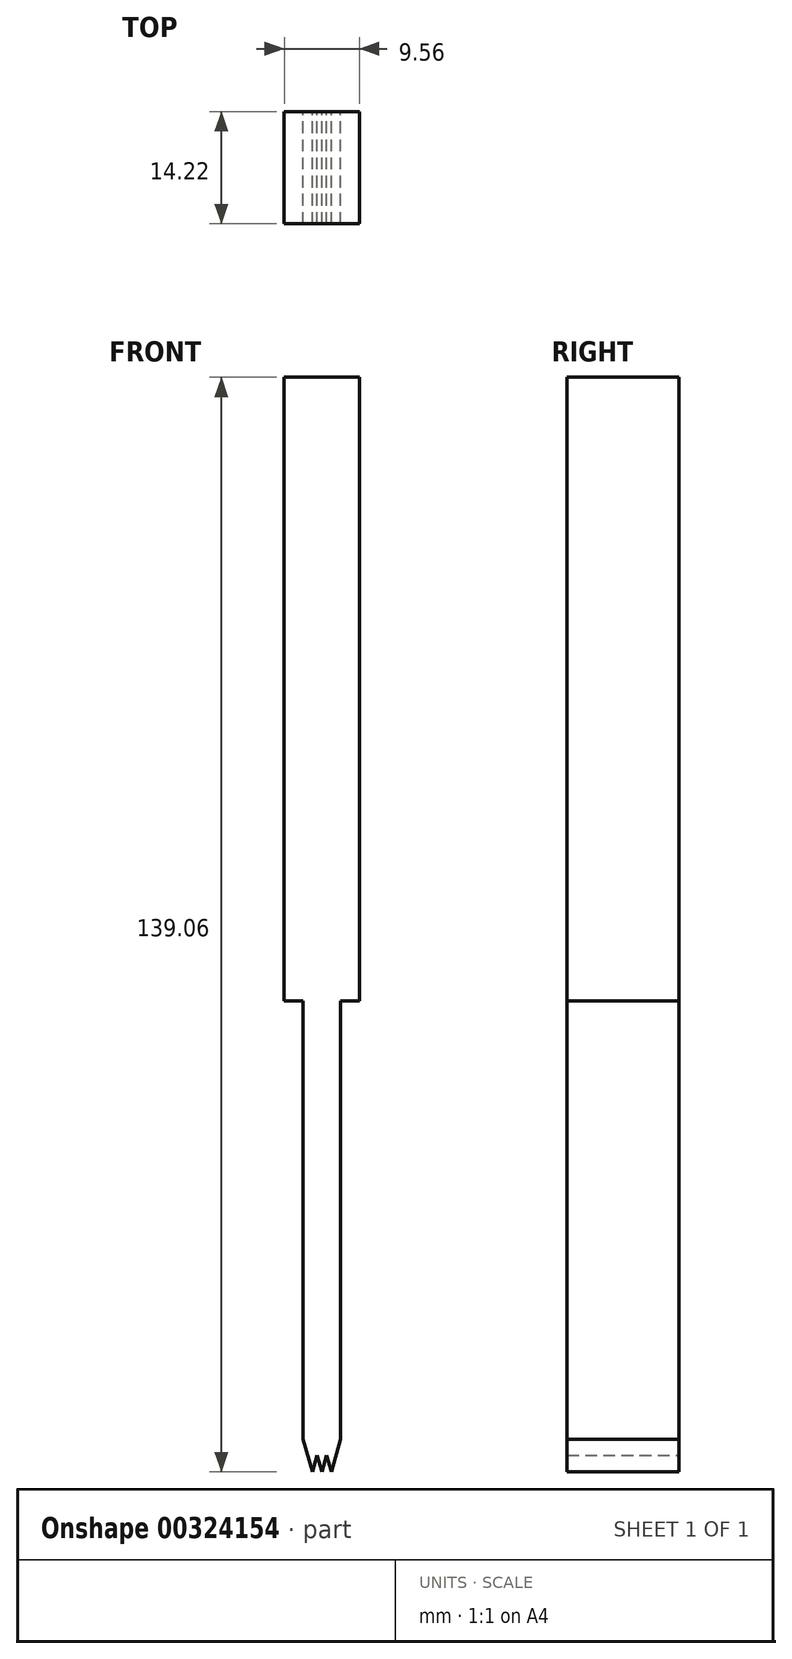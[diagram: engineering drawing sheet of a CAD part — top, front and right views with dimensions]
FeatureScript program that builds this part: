
annotation { "Feature Type Name" : "Feature", "Feature Type Description" : "" }
export const myFeature = defineFeature(function(context is Context, id is Id, definition is map)
    precondition{}
    {
        {
            var Q0;
            Q0=qCreatedBy(makeId("Front.planeOp"),FACE);
            var sketch = newSketch(context, id + "F0", { "sketchPlane" : qUnion([Q0])});
            skPoint(sketch, "E0.middle", {"position": v(0, 0) * mm});
            skLineSegment(sketch, "E1.bottom", {"start": v(-4.78, 39.63) * mm, "end": v(4.78, 39.63) * mm});
            skLineSegment(sketch, "E1.top", {"start": v(-4.78, -39.63) * mm, "end": v(4.78, -39.63) * mm});
            skLineSegment(sketch, "E1.left", {"start": v(-4.78, 39.63) * mm, "end": v(-4.78, -39.63) * mm});
            skLineSegment(sketch, "E1.right", {"start": v(4.78, 39.63) * mm, "end": v(4.78, -39.63) * mm});
            skLineSegment(sketch, "E2", {"start": v(-4.78, -39.63) * mm, "end": v(0, -39.63) * mm});
            skLineSegment(sketch, "E3", {"start": v(0, -39.63) * mm, "end": v(4.78, -39.63) * mm});
            skLineSegment(sketch, "E4", {"start": v(2.4, -39.63) * mm, "end": v(2.4, -95.29) * mm});
            skLineSegment(sketch, "E5", {"start": v(2.4, -95.29) * mm, "end": v(2.4, -39.63) * mm});
            skLineSegment(sketch, "E6", {"start": v(-2.4, -39.63) * mm, "end": v(-2.4, -95.29) * mm});
            skPoint(sketch, "E7.endSnap0", {"position": v(0, -95.29) * mm});
            skLineSegment(sketch, "E8", {"start": v(-2.4, -95.29) * mm, "end": v(-1.2, -99.43) * mm});
            skPoint(sketch, "E8.endSnap0", {"position": v(-1.2, -95.29) * mm});
            skLineSegment(sketch, "E9", {"start": v(-1.2, -99.43) * mm, "end": v(0, -95.29) * mm});
            skLineSegment(sketch, "E10", {"start": v(0, -95.29) * mm, "end": v(1.2, -99.43) * mm});
            skPoint(sketch, "E10.endSnap0", {"position": v(1.2, -95.29) * mm});
            skLineSegment(sketch, "E11", {"start": v(1.2, -99.43) * mm, "end": v(2.4, -95.29) * mm});
            skLineSegment(sketch, "E12", {"start": v(-1.2, -95.29) * mm, "end": v(0, -99.43) * mm});
            skLineSegment(sketch, "E13", {"start": v(0, -99.43) * mm, "end": v(1.2, -95.29) * mm});
            skSolve(sketch);
        }
        {
            var Q0;
            Q0 = qSketchRegion(id + "F0", true);
            extrude(context, id + "F1", {"entities" : qUnion([Q0]), "depth" : 14.22 * mm});
        }
    });
